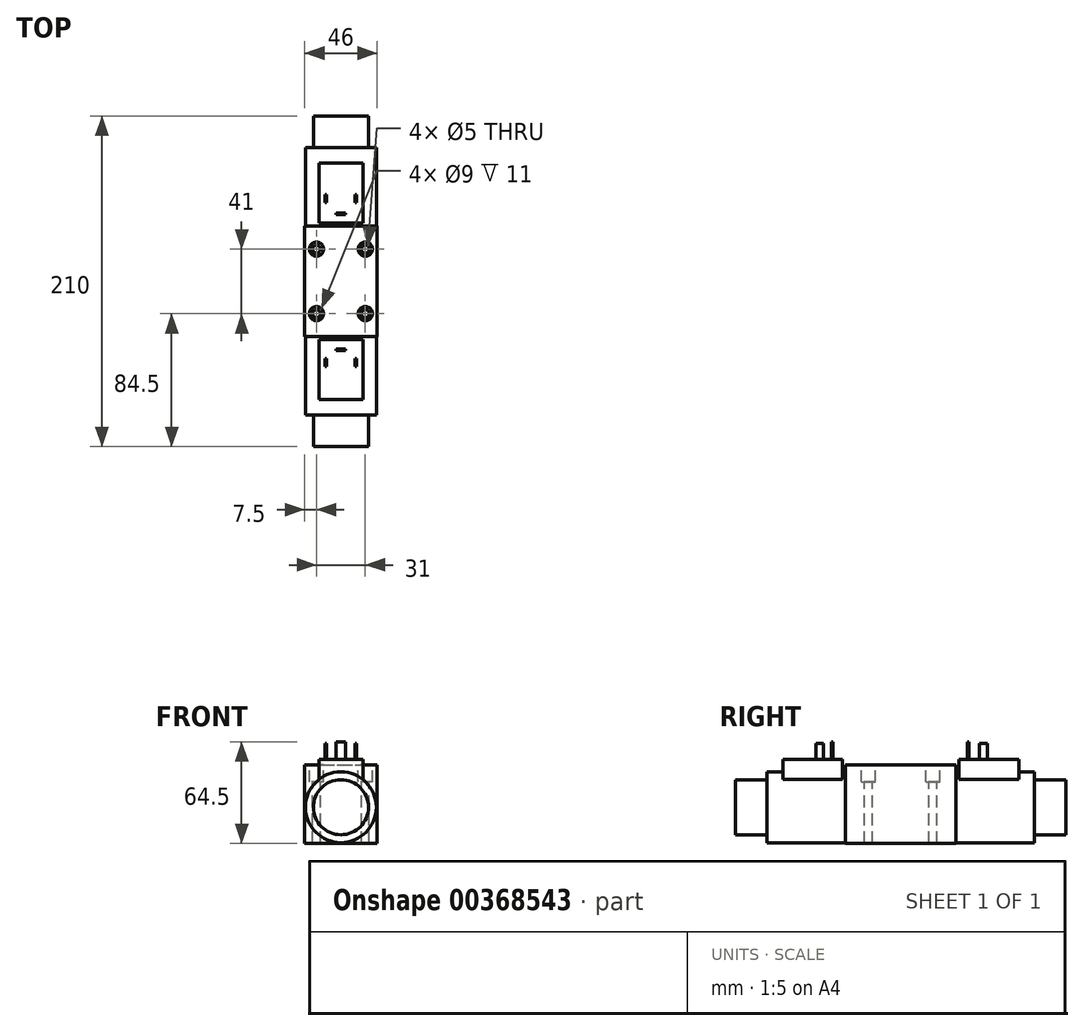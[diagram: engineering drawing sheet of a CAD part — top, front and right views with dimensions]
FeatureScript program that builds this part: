
annotation { "Feature Type Name" : "Feature", "Feature Type Description" : "" }
export const myFeature = defineFeature(function(context is Context, id is Id, definition is map)
    precondition{}
    {
        {
            var Q0;
            Q0=qCreatedBy(makeId("Front.planeOp"),FACE);
            var sketch = newSketch(context, id + "F0", { "sketchPlane" : qUnion([Q0])});
            skCircle(sketch, "E0", {"center": v(0, 0) * mm, "radius": 22.5 * mm});
            skSolve(sketch);
        }
        {
            var Q0;
            Q0=makeQuery(id+"F0.imprint","IMPRINT",FACE,{"disambiguationData":[TD([[makeQuery(id+"F0.imprint","IMPRINT",EDGE,{"derivedFrom":sQuery(id+"F0.wireOp",EDGE,"E0")}),1.0]])]});
            extrude(context, id + "F1", {"entities" : qUnion([Q0]), "depth" : 50 * mm});
        }
        {
            var Q0;
            Q0=makeQuery(id+"F1.opExtrude","CAP_FACE",FACE,{"disambiguationData":[OSD([sQuery(id+"F0.wireOp",EDGE,"E0")])],"isStart":false});
            var sketch = newSketch(context, id + "F2", { "sketchPlane" : qUnion([Q0])});
            skLineSegment(sketch, "E1.bottom", {"start": v(-23, 27) * mm, "end": v(23, 27) * mm});
            skLineSegment(sketch, "E1.top", {"start": v(-23, -23) * mm, "end": v(23, -23) * mm});
            skLineSegment(sketch, "E1.left", {"start": v(-23, 27) * mm, "end": v(-23, -23) * mm});
            skLineSegment(sketch, "E1.right", {"start": v(23, 27) * mm, "end": v(23, -23) * mm});
            skLineSegment(sketch, "E2", {"start": v(0, 0) * mm, "end": v(-81.57, 0) * mm, "construction": true});
            skSolve(sketch);
        }
        {
            var Q0;
            Q0=makeQuery(id+"F2.imprint","IMPRINT",FACE,{"disambiguationData":[TD([[makeQuery(id+"F2.imprint","IMPRINT",EDGE,{"derivedFrom":sQuery(id+"F2.wireOp",EDGE,"E1.bottom")}),-1.0]])]});
            var Q1;
            {var subQ0=sQuery(id+"F2.wireOp",EDGE,"E1.top");var subQ1=makeQuery(id+"F1.opExtrude","CAP_EDGE",EDGE,{"disambiguationData":[OSD([sQuery(id+"F0.wireOp",EDGE,"E0")])],"isStart":false});var subQ2=makeQuery(id+"F2.imprint","INTERSECT",VERTEX,{"disambiguationData":[OD(0.0)],"derivedFrom":[subQ1,subQ0]});Q1=makeQuery(id+"F2.imprint","IMPRINT",FACE,{"disambiguationData":[TD([[makeQuery(id+"F2.imprint","IMPRINT",EDGE,{"disambiguationData":[TD([[subQ2,-1.0]])],"derivedFrom":subQ0}),1.0]])]});}
            var Q2;
            Q2=makeQuery(id+"F2.imprint","IMPRINT",FACE,{"disambiguationData":[TD([[makeQuery(id+"F2.imprint","IMPRINT",EDGE,{"derivedFrom":makeQuery(id+"F1.opExtrude","CAP_EDGE",EDGE,{"disambiguationData":[OSD([sQuery(id+"F0.wireOp",EDGE,"E0")])],"isStart":false})}),1.0]])]});
            extrude(context, id + "F3", {"entities" : qUnion([Q0, Q1, Q2]), "operationType" : NewBodyOperationType.ADD, "depth" : 70 * mm});
        }
        {
            var Q0;
            Q0=makeQuery(id+"F3.opExtrude","CAP_FACE",FACE,{"disambiguationData":[OSD([sQuery(id+"F2.wireOp",EDGE,"E1.bottom"),sQuery(id+"F2.wireOp",EDGE,"E1.top"),sQuery(id+"F2.wireOp",EDGE,"E1.left"),sQuery(id+"F2.wireOp",EDGE,"E1.right")])],"isStart":false});
            var sketch = newSketch(context, id + "F4", { "sketchPlane" : qUnion([Q0])});
            skCircle(sketch, "E3", {"center": v(0, 0) * mm, "radius": 22.5 * mm});
            skLineSegment(sketch, "E4", {"start": v(0, 0) * mm, "end": v(-34.84, 0) * mm, "construction": true});
            skSolve(sketch);
        }
        {
            var Q0;
            {var subQ0=sQuery(id+"F4.wireOp",EDGE,"E3");var subQ1=makeQuery(id+"F3.opExtrude","CAP_EDGE",EDGE,{"disambiguationData":[OSD([sQuery(id+"F2.wireOp",EDGE,"E1.top")])],"isStart":false});var subQ2=makeQuery(id+"F4.imprint","INTERSECT",VERTEX,{"disambiguationData":[OD(0.0)],"derivedFrom":[subQ1,subQ0]});Q0=makeQuery(id+"F4.imprint","IMPRINT",FACE,{"disambiguationData":[TD([[makeQuery(id+"F4.imprint","IMPRINT",EDGE,{"disambiguationData":[TD([[subQ2,1.0]])],"derivedFrom":subQ0}),1.0]])]});}
            extrude(context, id + "F5", {"entities" : qUnion([Q0]), "operationType" : NewBodyOperationType.ADD, "depth" : 50 * mm});
        }
        {
            var Q0;
            Q0=makeQuery(id+"F5.opExtrude","CAP_FACE",FACE,{"disambiguationData":[OSD([sQuery(id+"F2.wireOp",EDGE,"E1.top"),sQuery(id+"F4.wireOp",EDGE,"E3")])],"isStart":false});
            var sketch = newSketch(context, id + "F6", { "sketchPlane" : qUnion([Q0])});
            skCircle(sketch, "E5", {"center": v(0, 0) * mm, "radius": 17.5 * mm});
            skSolve(sketch);
        }
        {
            var Q0;
            Q0=makeQuery(id+"F6.imprint","IMPRINT",FACE,{"disambiguationData":[TD([[makeQuery(id+"F6.imprint","IMPRINT",EDGE,{"derivedFrom":sQuery(id+"F6.wireOp",EDGE,"E5")}),1.0]])]});
            extrude(context, id + "F7", {"entities" : qUnion([Q0]), "operationType" : NewBodyOperationType.ADD, "depth" : 20 * mm});
        }
        {
            var Q0;
            Q0=makeQuery(id+"F1.opExtrude","CAP_FACE",FACE,{"disambiguationData":[OSD([sQuery(id+"F0.wireOp",EDGE,"E0")])],"isStart":true});
            var sketch = newSketch(context, id + "F8", { "sketchPlane" : qUnion([Q0])});
            skCircle(sketch, "E6", {"center": v(0, 0) * mm, "radius": 17.5 * mm});
            skSolve(sketch);
        }
        {
            var Q0;
            Q0=makeQuery(id+"F8.imprint","IMPRINT",FACE,{"disambiguationData":[TD([[makeQuery(id+"F8.imprint","IMPRINT",EDGE,{"derivedFrom":sQuery(id+"F8.wireOp",EDGE,"E6")}),1.0]])]});
            extrude(context, id + "F9", {"entities" : qUnion([Q0]), "operationType" : NewBodyOperationType.ADD, "depth" : 20 * mm});
        }
        {
            var Q0;
            Q0=qCreatedBy(makeId("Top.planeOp"),FACE);
            var sketch = newSketch(context, id + "F10", { "sketchPlane" : qUnion([Q0])});
            skLineSegment(sketch, "E7.bottom", {"start": v(-14, -48) * mm, "end": v(14, -48) * mm});
            skLineSegment(sketch, "E7.top", {"start": v(-14, -10) * mm, "end": v(14, -10) * mm});
            skLineSegment(sketch, "E7.left", {"start": v(-14, -48) * mm, "end": v(-14, -10) * mm});
            skLineSegment(sketch, "E7.right", {"start": v(14, -48) * mm, "end": v(14, -10) * mm});
            skLineSegment(sketch, "E8", {"start": v(0, 0) * mm, "end": v(0, 34.53) * mm, "construction": true});
            skSolve(sketch);
        }
        {
            var Q0;
            Q0 = qSketchRegion(id + "F10", true);
            extrude(context, id + "F11", {"entities" : qUnion([Q0]), "operationType" : NewBodyOperationType.ADD, "depth" : 30.5 * mm});
        }
        {
            var Q0;
            Q0=qCreatedBy(makeId("Top.planeOp"),FACE);
            var sketch = newSketch(context, id + "F12", { "sketchPlane" : qUnion([Q0])});
            skLineSegment(sketch, "E9.bottom", {"start": v(14, -160) * mm, "end": v(-14, -160) * mm});
            skLineSegment(sketch, "E9.top", {"start": v(14, -122) * mm, "end": v(-14, -122) * mm});
            skLineSegment(sketch, "E9.left", {"start": v(14, -160) * mm, "end": v(14, -122) * mm});
            skLineSegment(sketch, "E9.right", {"start": v(-14, -160) * mm, "end": v(-14, -122) * mm});
            skLineSegment(sketch, "E10", {"start": v(0, -117.74) * mm, "end": v(0, -183.85) * mm, "construction": true});
            skSolve(sketch);
        }
        {
            var Q0;
            Q0 = qSketchRegion(id + "F12", true);
            extrude(context, id + "F13", {"entities" : qUnion([Q0]), "operationType" : NewBodyOperationType.ADD, "depth" : 30.5 * mm});
        }
        {
            var Q0;
            Q0=makeQuery(id+"F3.opExtrude","SWEPT_FACE",FACE,{"disambiguationData":[OSD([sQuery(id+"F2.wireOp",EDGE,"E1.bottom")])]});
            var sketch = newSketch(context, id + "F14", { "sketchPlane" : qUnion([Q0])});
            skCircle(sketch, "E11", {"center": v(-15.5, -64.5) * mm, "radius": 4.5 * mm});
            skCircle(sketch, "E12", {"center": v(15.5, -64.5) * mm, "radius": 4.5 * mm});
            skCircle(sketch, "E13", {"center": v(15.5, -105.5) * mm, "radius": 4.5 * mm});
            skCircle(sketch, "E14", {"center": v(-15.5, -105.5) * mm, "radius": 4.5 * mm});
            skSolve(sketch);
        }
        {
            var Q0;
            Q0=makeQuery(id+"F14.imprint","IMPRINT",FACE,{"disambiguationData":[TD([[makeQuery(id+"F14.imprint","IMPRINT",EDGE,{"derivedFrom":sQuery(id+"F14.wireOp",EDGE,"E11")}),-1.0]])]});
            var sketch = newSketch(context, id + "F15", { "sketchPlane" : qUnion([Q0])});
            skCircle(sketch, "E15", {"center": v(-15.5, -64.5) * mm, "radius": 2.5 * mm});
            skCircle(sketch, "E16", {"center": v(-15.5, -105.5) * mm, "radius": 2.5 * mm});
            skCircle(sketch, "E17", {"center": v(15.5, -105.5) * mm, "radius": 2.5 * mm});
            skCircle(sketch, "E18", {"center": v(15.5, -64.5) * mm, "radius": 2.5 * mm});
            skSolve(sketch);
        }
        {
            var Q0;
            Q0 = qSketchRegion(id + "F15", true);
            extrude(context, id + "F16", {"entities" : qUnion([Q0]), "operationType" : NewBodyOperationType.REMOVE, "oppositeDirection" : true, "depth" : 50 * mm});
        }
        {
            var Q0;
            Q0 = qSketchRegion(id + "F14", true);
            extrude(context, id + "F17", {"entities" : qUnion([Q0]), "operationType" : NewBodyOperationType.REMOVE, "oppositeDirection" : true, "depth" : 11 * mm});
        }
        {
            var Q0;
            Q0=makeQuery(id+"F11.opExtrude","CAP_FACE",FACE,{"disambiguationData":[OSD([sQuery(id+"F10.wireOp",EDGE,"E7.bottom"),sQuery(id+"F10.wireOp",EDGE,"E7.top"),sQuery(id+"F10.wireOp",EDGE,"E7.left"),sQuery(id+"F10.wireOp",EDGE,"E7.right")])],"isStart":false});
            var sketch = newSketch(context, id + "F18", { "sketchPlane" : qUnion([Q0])});
            skLineSegment(sketch, "E19.bottom", {"start": v(-10, -35) * mm, "end": v(-9.1, -35) * mm});
            skLineSegment(sketch, "E19.top", {"start": v(-10, -30) * mm, "end": v(-9.1, -30) * mm});
            skLineSegment(sketch, "E19.left", {"start": v(-10, -35) * mm, "end": v(-10, -30) * mm});
            skLineSegment(sketch, "E19.right", {"start": v(-9.1, -35) * mm, "end": v(-9.1, -30) * mm});
            skLineSegment(sketch, "E20.bottom", {"start": v(9.1, -35) * mm, "end": v(10, -35) * mm});
            skLineSegment(sketch, "E20.top", {"start": v(9.1, -30) * mm, "end": v(10, -30) * mm});
            skLineSegment(sketch, "E20.left", {"start": v(9.1, -35) * mm, "end": v(9.1, -30) * mm});
            skLineSegment(sketch, "E20.right", {"start": v(10, -35) * mm, "end": v(10, -30) * mm});
            skLineSegment(sketch, "E21.bottom", {"start": v(3, -42.62) * mm, "end": v(-3, -42.62) * mm});
            skLineSegment(sketch, "E21.top", {"start": v(3, -41.71) * mm, "end": v(-3, -41.71) * mm});
            skLineSegment(sketch, "E21.left", {"start": v(3, -42.62) * mm, "end": v(3, -41.71) * mm});
            skLineSegment(sketch, "E21.right", {"start": v(-3, -42.62) * mm, "end": v(-3, -41.71) * mm});
            skSolve(sketch);
        }
        {
            var Q0;
            Q0=makeQuery(id+"F18.imprint","IMPRINT",FACE,{"disambiguationData":[TD([[makeQuery(id+"F18.imprint","IMPRINT",EDGE,{"derivedFrom":sQuery(id+"F18.wireOp",EDGE,"E21.bottom")}),-1.0]])]});
            extrude(context, id + "F19", {"entities" : qUnion([Q0]), "operationType" : NewBodyOperationType.ADD, "depth" : 11 * mm});
        }
        {
            var Q0;
            Q0=makeQuery(id+"F13.opExtrude","CAP_FACE",FACE,{"disambiguationData":[OSD([sQuery(id+"F12.wireOp",EDGE,"E9.bottom"),sQuery(id+"F12.wireOp",EDGE,"E9.top"),sQuery(id+"F12.wireOp",EDGE,"E9.left"),sQuery(id+"F12.wireOp",EDGE,"E9.right")])],"isStart":false});
            var sketch = newSketch(context, id + "F20", { "sketchPlane" : qUnion([Q0])});
            skLineSegment(sketch, "E22.bottom", {"start": v(9, -139) * mm, "end": v(10, -139) * mm});
            skLineSegment(sketch, "E22.top", {"start": v(9, -134) * mm, "end": v(10, -134) * mm});
            skLineSegment(sketch, "E22.left", {"start": v(9, -139) * mm, "end": v(9, -134) * mm});
            skLineSegment(sketch, "E22.right", {"start": v(10, -139) * mm, "end": v(10, -134) * mm});
            skLineSegment(sketch, "E23.bottom", {"start": v(3, -128) * mm, "end": v(-3, -128) * mm});
            skLineSegment(sketch, "E23.top", {"start": v(3, -129) * mm, "end": v(-3, -129) * mm});
            skLineSegment(sketch, "E23.left", {"start": v(3, -128) * mm, "end": v(3, -129) * mm});
            skLineSegment(sketch, "E23.right", {"start": v(-3, -128) * mm, "end": v(-3, -129) * mm});
            skLineSegment(sketch, "E24.bottom", {"start": v(-10, -134) * mm, "end": v(-9, -134) * mm});
            skLineSegment(sketch, "E24.top", {"start": v(-10, -139) * mm, "end": v(-9, -139) * mm});
            skLineSegment(sketch, "E24.left", {"start": v(-10, -134) * mm, "end": v(-10, -139) * mm});
            skLineSegment(sketch, "E24.right", {"start": v(-9, -134) * mm, "end": v(-9, -139) * mm});
            skSolve(sketch);
        }
        {
            var Q0;
            Q0=makeQuery(id+"F20.imprint","IMPRINT",FACE,{"disambiguationData":[TD([[makeQuery(id+"F20.imprint","IMPRINT",EDGE,{"derivedFrom":sQuery(id+"F20.wireOp",EDGE,"E23.bottom")}),1.0]])]});
            extrude(context, id + "F21", {"entities" : qUnion([Q0]), "operationType" : NewBodyOperationType.ADD, "depth" : 11 * mm});
        }
        {
            var Q0;
            Q0 = qSketchRegion(id + "F20", true);
            extrude(context, id + "F22", {"entities" : qUnion([Q0]), "operationType" : NewBodyOperationType.ADD, "depth" : 10 * mm});
        }
        {
            var Q0;
            Q0 = qSketchRegion(id + "F18", true);
            extrude(context, id + "F23", {"entities" : qUnion([Q0]), "operationType" : NewBodyOperationType.ADD, "depth" : 10 * mm});
        }
    });
